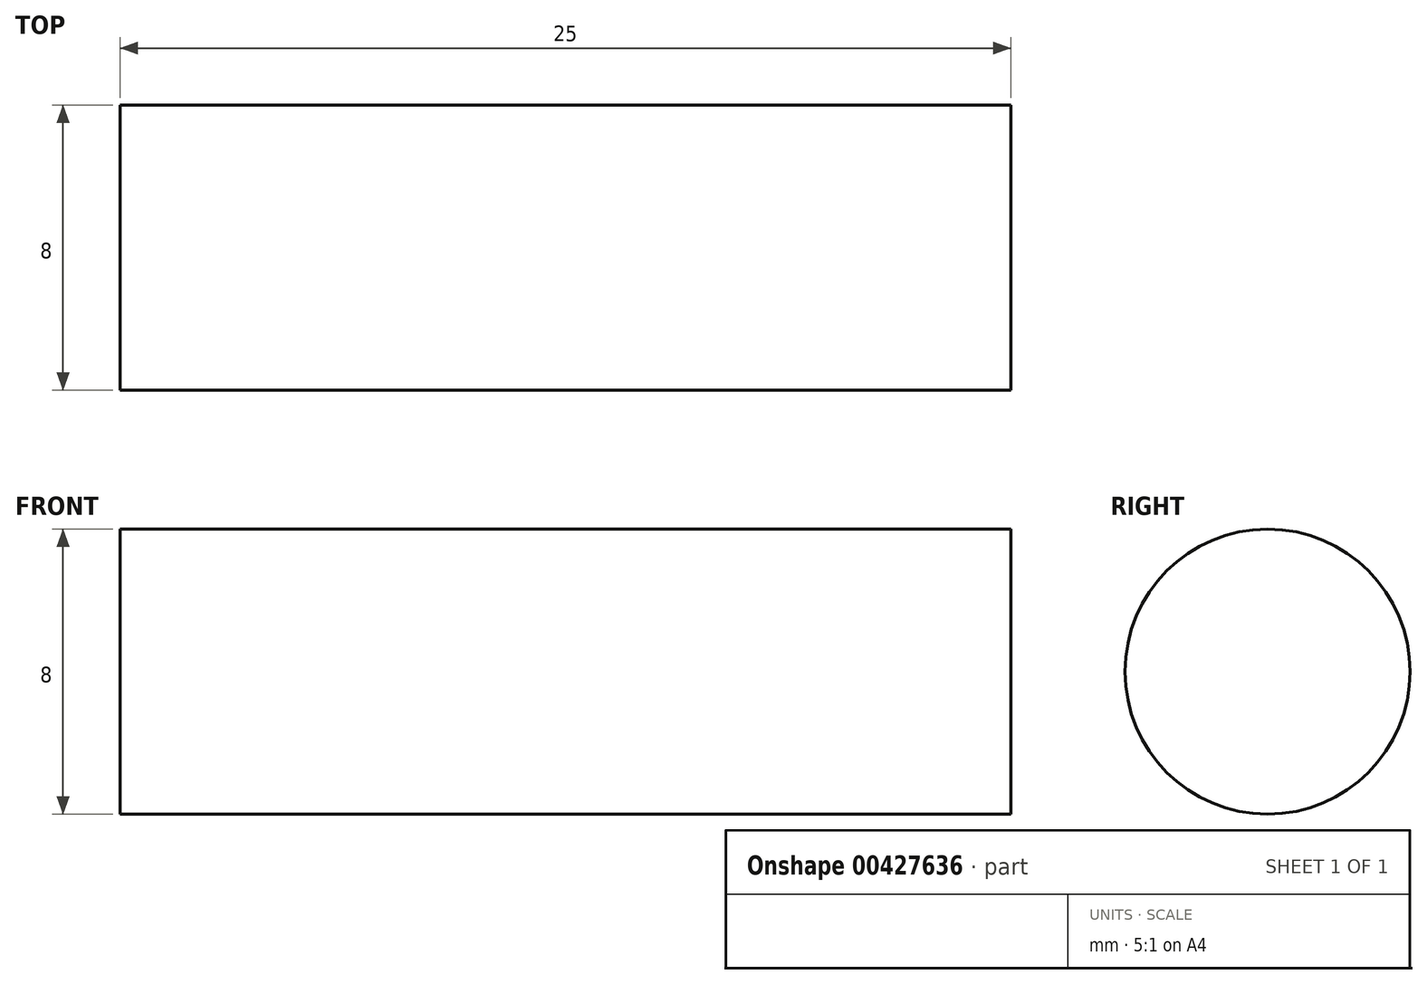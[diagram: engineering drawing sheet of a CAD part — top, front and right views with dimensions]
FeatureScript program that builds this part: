
annotation { "Feature Type Name" : "Feature", "Feature Type Description" : "" }
export const myFeature = defineFeature(function(context is Context, id is Id, definition is map)
    precondition{}
    {
        {
            var Q0;
            Q0=qCreatedBy(makeId("Right.planeOp"),FACE);
            var sketch = newSketch(context, id + "F0", { "sketchPlane" : qUnion([Q0])});
            skCircle(sketch, "E0", {"center": v(0, 0) * mm, "radius": 4 * mm});
            skSolve(sketch);
        }
        {
            var Q0;
            Q0 = qSketchRegion(id + "F0", true);
            extrude(context, id + "F1", {"entities" : qUnion([Q0]), "depth" : 25 * mm});
        }
    });
